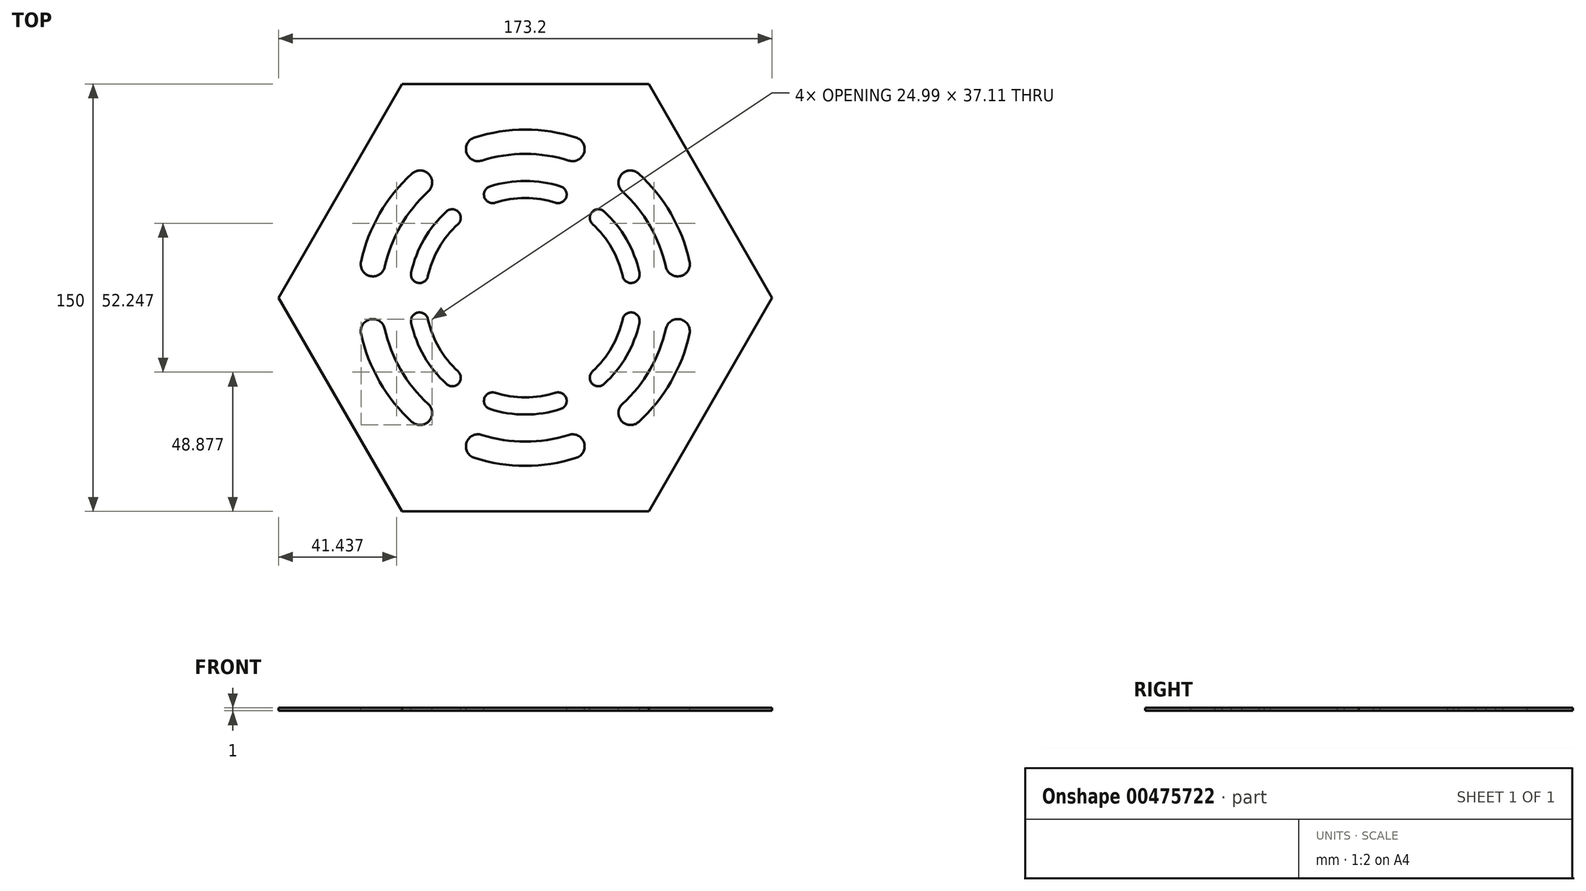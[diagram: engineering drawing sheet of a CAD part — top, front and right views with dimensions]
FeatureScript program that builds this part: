
annotation { "Feature Type Name" : "Feature", "Feature Type Description" : "" }
export const myFeature = defineFeature(function(context is Context, id is Id, definition is map)
    precondition{}
    {
        {
            var Q0;
            Q0=qCreatedBy(makeId("Top.planeOp"),FACE);
            var sketch = newSketch(context, id + "F0", { "sketchPlane" : qUnion([Q0])});
            skCircle(sketch, "E0.cCircle", {"center": v(0, 0) * mm, "radius": 75 * mm, "construction": true});
            skLineSegment(sketch, "E0.0", {"start": v(43.3, 75) * mm, "end": v(86.6, 0) * mm});
            skLineSegment(sketch, "E0.1", {"start": v(86.6, 0) * mm, "end": v(43.3, -75) * mm});
            skLineSegment(sketch, "E0.2", {"start": v(43.3, -75) * mm, "end": v(-43.3, -75) * mm});
            skLineSegment(sketch, "E0.3", {"start": v(-43.3, -75) * mm, "end": v(-86.6, 0) * mm});
            skLineSegment(sketch, "E0.4", {"start": v(-86.6, 0) * mm, "end": v(-43.3, 75) * mm});
            skLineSegment(sketch, "E0.5", {"start": v(-43.3, 75) * mm, "end": v(43.3, 75) * mm});
            skPoint(sketch, "E0.0.midPoint", {"position": v(64.95, 37.5) * mm});
            skSolve(sketch);
        }
        {
            var Q0;
            Q0=qSketchRegion(id+"F0",true);
            extrude(context, id + "F1", {"entities" : qUnion([Q0]), "depth" : 1 * mm});
        }
        {
            var Q0;
            Q0=makeQuery(id+"F1.opExtrude","CAP_FACE",FACE,{"disambiguationData":[OSD([sQuery(id+"F0.wireOp",EDGE,"E0.0"),sQuery(id+"F0.wireOp",EDGE,"E0.1"),sQuery(id+"F0.wireOp",EDGE,"E0.2"),sQuery(id+"F0.wireOp",EDGE,"E0.3"),sQuery(id+"F0.wireOp",EDGE,"E0.4"),sQuery(id+"F0.wireOp",EDGE,"E0.5")])],"isStart":false});
            var sketch = newSketch(context, id + "F2", { "sketchPlane" : qUnion([Q0])});
            skArc(sketch, "E1", {"start": v(57.63, 12.66) * mm, "mid": v(51.1, 29.5) * mm, "end": v(39.78, 43.57) * mm});
            skLineSegment(sketch, "E2", {"start": v(0, 0) * mm, "end": v(39.78, 43.57) * mm, "construction": true});
            skLineSegment(sketch, "E3", {"start": v(0, 0) * mm, "end": v(57.63, 12.66) * mm, "construction": true});
            skArc(sketch, "E4", {"start": v(49.32, 10.84) * mm, "mid": v(43.73, 25.25) * mm, "end": v(34.05, 37.3) * mm});
            skCircle(sketch, "E5", {"center": v(36.91, 40.44) * mm, "radius": 4.25 * mm});
            skCircle(sketch, "E6", {"center": v(53.47, 11.75) * mm, "radius": 4.25 * mm});
            skCircle(sketch, "E7.1.0", {"center": v(-16.56, 52.19) * mm, "radius": 4.25 * mm});
            skArc(sketch, "E7.1.1", {"start": v(17.85, 56.24) * mm, "mid": v(0, 59) * mm, "end": v(-17.85, 56.24) * mm});
            skArc(sketch, "E7.1.2", {"start": v(15.28, 48.13) * mm, "mid": v(0, 50.5) * mm, "end": v(-15.28, 48.13) * mm});
            skCircle(sketch, "E7.1.3", {"center": v(16.56, 52.19) * mm, "radius": 4.25 * mm});
            skCircle(sketch, "E7.2.0", {"center": v(-53.47, 11.75) * mm, "radius": 4.25 * mm});
            skArc(sketch, "E7.2.1", {"start": v(-39.78, 43.57) * mm, "mid": v(-51.1, 29.5) * mm, "end": v(-57.63, 12.66) * mm});
            skArc(sketch, "E7.2.2", {"start": v(-34.05, 37.3) * mm, "mid": v(-43.73, 25.25) * mm, "end": v(-49.32, 10.84) * mm});
            skCircle(sketch, "E7.2.3", {"center": v(-36.91, 40.44) * mm, "radius": 4.25 * mm});
            skCircle(sketch, "E7.3.0", {"center": v(-36.91, -40.44) * mm, "radius": 4.25 * mm});
            skArc(sketch, "E7.3.1", {"start": v(-57.63, -12.66) * mm, "mid": v(-51.1, -29.5) * mm, "end": v(-39.78, -43.57) * mm});
            skArc(sketch, "E7.3.2", {"start": v(-49.32, -10.84) * mm, "mid": v(-43.73, -25.25) * mm, "end": v(-34.05, -37.3) * mm});
            skCircle(sketch, "E7.3.3", {"center": v(-53.47, -11.75) * mm, "radius": 4.25 * mm});
            skCircle(sketch, "E7.4.0", {"center": v(16.56, -52.19) * mm, "radius": 4.25 * mm});
            skArc(sketch, "E7.4.1", {"start": v(-17.85, -56.24) * mm, "mid": v(0, -59) * mm, "end": v(17.85, -56.24) * mm});
            skArc(sketch, "E7.4.2", {"start": v(-15.28, -48.13) * mm, "mid": v(0, -50.5) * mm, "end": v(15.28, -48.13) * mm});
            skCircle(sketch, "E7.4.3", {"center": v(-16.56, -52.19) * mm, "radius": 4.25 * mm});
            skCircle(sketch, "E7.5.0", {"center": v(53.47, -11.75) * mm, "radius": 4.25 * mm});
            skArc(sketch, "E7.5.1", {"start": v(39.78, -43.57) * mm, "mid": v(51.1, -29.5) * mm, "end": v(57.63, -12.66) * mm});
            skArc(sketch, "E7.5.2", {"start": v(34.05, -37.3) * mm, "mid": v(43.73, -25.25) * mm, "end": v(49.32, -10.84) * mm});
            skCircle(sketch, "E7.5.3", {"center": v(36.91, -40.44) * mm, "radius": 4.25 * mm});
            skLineSegment(sketch, "E8", {"start": v(53.47, 11.75) * mm, "end": v(53.47, -11.75) * mm, "construction": true});
            skPoint(sketch, "E9", {"position": v(53.47, 7.5) * mm});
            skPoint(sketch, "E10", {"position": v(53.47, -7.5) * mm});
            skArc(sketch, "E11", {"start": v(40.04, 8.8) * mm, "mid": v(35.5, 20.5) * mm, "end": v(27.64, 30.28) * mm});
            skArc(sketch, "E12", {"start": v(34.18, 7.51) * mm, "mid": v(30.31, 17.5) * mm, "end": v(23.6, 25.85) * mm});
            skCircle(sketch, "E13", {"center": v(37.11, 8.16) * mm, "radius": 3 * mm});
            skCircle(sketch, "E14", {"center": v(25.62, 28.06) * mm, "radius": 3 * mm});
            skCircle(sketch, "E15.1.0", {"center": v(-11.5, 36.22) * mm, "radius": 3 * mm});
            skArc(sketch, "E15.1.1", {"start": v(12.4, 39.08) * mm, "mid": v(0, 41) * mm, "end": v(-12.4, 39.08) * mm});
            skCircle(sketch, "E15.1.2", {"center": v(11.5, 36.22) * mm, "radius": 3 * mm});
            skArc(sketch, "E15.1.3", {"start": v(10.59, 33.36) * mm, "mid": v(0, 35) * mm, "end": v(-10.59, 33.36) * mm});
            skCircle(sketch, "E15.2.0", {"center": v(-37.11, 8.16) * mm, "radius": 3 * mm});
            skArc(sketch, "E15.2.1", {"start": v(-27.64, 30.28) * mm, "mid": v(-35.5, 20.5) * mm, "end": v(-40.04, 8.8) * mm});
            skCircle(sketch, "E15.2.2", {"center": v(-25.62, 28.06) * mm, "radius": 3 * mm});
            skArc(sketch, "E15.2.3", {"start": v(-23.6, 25.85) * mm, "mid": v(-30.31, 17.5) * mm, "end": v(-34.18, 7.51) * mm});
            skCircle(sketch, "E15.3.0", {"center": v(-25.62, -28.06) * mm, "radius": 3 * mm});
            skArc(sketch, "E15.3.1", {"start": v(-40.04, -8.8) * mm, "mid": v(-35.5, -20.5) * mm, "end": v(-27.64, -30.28) * mm});
            skCircle(sketch, "E15.3.2", {"center": v(-37.11, -8.16) * mm, "radius": 3 * mm});
            skArc(sketch, "E15.3.3", {"start": v(-34.18, -7.51) * mm, "mid": v(-30.31, -17.5) * mm, "end": v(-23.6, -25.85) * mm});
            skCircle(sketch, "E15.4.0", {"center": v(11.5, -36.22) * mm, "radius": 3 * mm});
            skArc(sketch, "E15.4.1", {"start": v(-12.4, -39.08) * mm, "mid": v(0, -41) * mm, "end": v(12.4, -39.08) * mm});
            skCircle(sketch, "E15.4.2", {"center": v(-11.5, -36.22) * mm, "radius": 3 * mm});
            skArc(sketch, "E15.4.3", {"start": v(-10.59, -33.36) * mm, "mid": v(0, -35) * mm, "end": v(10.59, -33.36) * mm});
            skCircle(sketch, "E15.5.0", {"center": v(37.11, -8.16) * mm, "radius": 3 * mm});
            skArc(sketch, "E15.5.1", {"start": v(27.64, -30.28) * mm, "mid": v(35.5, -20.5) * mm, "end": v(40.04, -8.8) * mm});
            skCircle(sketch, "E15.5.2", {"center": v(25.62, -28.06) * mm, "radius": 3 * mm});
            skArc(sketch, "E15.5.3", {"start": v(23.6, -25.85) * mm, "mid": v(30.31, -17.5) * mm, "end": v(34.18, -7.51) * mm});
            skSolve(sketch);
        }
        {
            var Q0;
            Q0=qSketchRegion(id+"F2",true);
            extrude(context, id + "F3", {"entities" : qUnion([Q0]), "operationType" : NewBodyOperationType.REMOVE, "endBound" : BoundingType.THROUGH_ALL, "oppositeDirection" : true, "depth" : 25 * mm});
        }
    });
